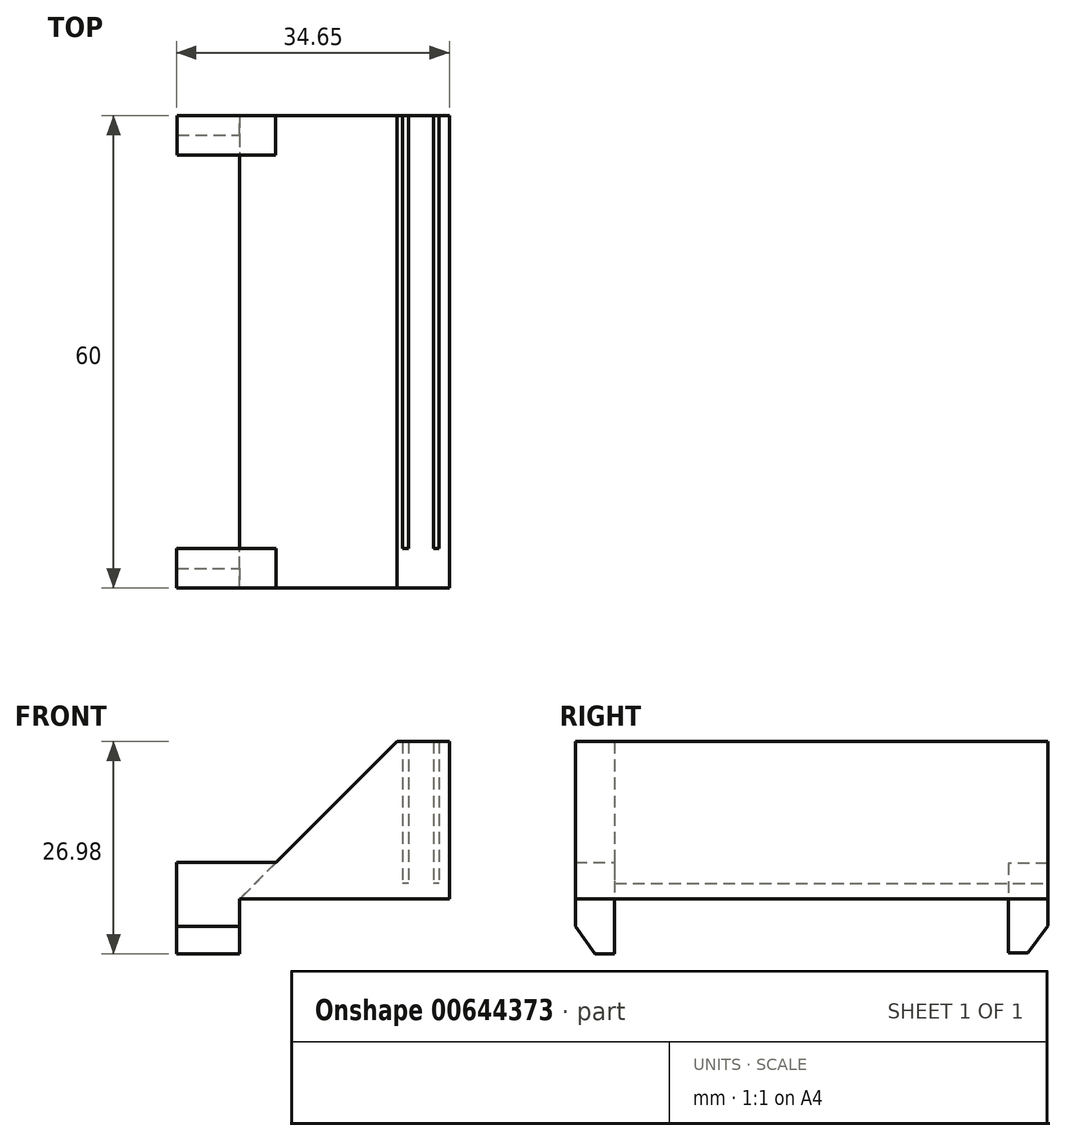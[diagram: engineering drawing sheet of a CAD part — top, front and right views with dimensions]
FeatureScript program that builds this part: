
annotation { "Feature Type Name" : "Feature", "Feature Type Description" : "" }
export const myFeature = defineFeature(function(context is Context, id is Id, definition is map)
    precondition{}
    {
        {
            var Q0;
            Q0=qCreatedBy(makeId("Front.planeOp"),FACE);
            var sketch = newSketch(context, id + "F0", { "sketchPlane" : qUnion([Q0])});
            skLineSegment(sketch, "E0", {"start": v(0.8, 1.7) * mm, "end": v(20.8, 1.7) * mm});
            skLineSegment(sketch, "E1", {"start": v(20.8, 1.7) * mm, "end": v(20.8, 21.7) * mm});
            skLineSegment(sketch, "E2", {"start": v(20.8, 21.7) * mm, "end": v(0.8, 1.7) * mm});
            skSolve(sketch);
        }
        {
            var Q0;
            Q0 = qSketchRegion(id + "F0", true);
            extrude(context, id + "F1", {"entities" : qUnion([Q0]), "depth" : 50 * mm, "offsetDistance" : 25 * mm});
        }
        {
            var Q0;
            Q0=makeQuery(id+"F1.opExtrude","CAP_FACE",FACE,{"disambiguationData":[OSD([sQuery(id+"F0.wireOp",EDGE,"E0"),sQuery(id+"F0.wireOp",EDGE,"E1"),sQuery(id+"F0.wireOp",EDGE,"E2")])],"isStart":true});
            var sketch = newSketch(context, id + "F2", { "sketchPlane" : qUnion([Q0])});
            skLineSegment(sketch, "E3", {"start": v(-20.8, 6.23) * mm, "end": v(7.12, 6.23) * mm});
            skLineSegment(sketch, "E4", {"start": v(7.12, 6.23) * mm, "end": v(7.12, -5.17) * mm});
            skLineSegment(sketch, "E5", {"start": v(7.12, -5.17) * mm, "end": v(-0.8, -5.17) * mm});
            skLineSegment(sketch, "E6", {"start": v(-0.8, -5.17) * mm, "end": v(-0.8, 1.7) * mm});
            skLineSegment(sketch, "E7", {"start": v(-0.8, 1.7) * mm, "end": v(-20.8, 1.7) * mm});
            skLineSegment(sketch, "E8", {"start": v(-20.8, 1.7) * mm, "end": v(-20.8, 6.23) * mm});
            skSolve(sketch);
        }
        {
            var Q0;
            {var subQ1=sQuery(id+"F2.wireOp",EDGE,"E4");Q0=makeQuery(id+"F2.imprint","IMPRINT",FACE,{"disambiguationData":[TD([[makeQuery(id+"F2.imprint","IMPRINT",EDGE,{"derivedFrom":subQ1}),-1.0]])]});}
            var Q1;
            {var subQ4=sQuery(id+"F2.wireOp",EDGE,"E7");Q1=makeQuery(id+"F2.imprint","IMPRINT",FACE,{"disambiguationData":[TD([[makeQuery(id+"F2.imprint","IMPRINT",EDGE,{"derivedFrom":subQ4}),-1.0]])]});}
            extrude(context, id + "F3", {"entities" : qUnion([Q0, Q1]), "operationType" : NewBodyOperationType.ADD, "depth" : 5 * mm, "offsetDistance" : 25 * mm});
        }
        {
            var Q0;
            Q0=makeQuery(id+"F1.opExtrude","CAP_FACE",FACE,{"disambiguationData":[OSD([sQuery(id+"F0.wireOp",EDGE,"E0"),sQuery(id+"F0.wireOp",EDGE,"E1"),sQuery(id+"F0.wireOp",EDGE,"E2")])],"isStart":false});
            var sketch = newSketch(context, id + "F4", { "sketchPlane" : qUnion([Q0])});
            skLineSegment(sketch, "E9", {"start": v(0.8, 1.7) * mm, "end": v(20.8, 1.7) * mm});
            skLineSegment(sketch, "E10", {"start": v(20.8, 1.7) * mm, "end": v(20.8, 6.3) * mm});
            skLineSegment(sketch, "E11", {"start": v(20.8, 6.3) * mm, "end": v(-7.22, 6.3) * mm});
            skLineSegment(sketch, "E12", {"start": v(-7.22, 6.3) * mm, "end": v(-7.22, -5.3) * mm});
            skLineSegment(sketch, "E13", {"start": v(-7.22, -5.3) * mm, "end": v(0.8, -5.3) * mm});
            skLineSegment(sketch, "E14", {"start": v(0.8, -5.3) * mm, "end": v(0.8, 1.7) * mm});
            skSolve(sketch);
        }
        {
            var Q0;
            {var subQ0=sQuery(id+"F4.wireOp",EDGE,"E9");Q0=makeQuery(id+"F4.imprint","IMPRINT",FACE,{"disambiguationData":[TD([[makeQuery(id+"F4.imprint","IMPRINT",EDGE,{"derivedFrom":subQ0}),1.0]])]});}
            var Q1;
            {var subQ1=sQuery(id+"F4.wireOp",EDGE,"E12");Q1=makeQuery(id+"F4.imprint","IMPRINT",FACE,{"disambiguationData":[TD([[makeQuery(id+"F4.imprint","IMPRINT",EDGE,{"derivedFrom":subQ1}),1.0]])]});}
            extrude(context, id + "F5", {"entities" : qUnion([Q0, Q1]), "operationType" : NewBodyOperationType.ADD, "depth" : 5 * mm, "offsetDistance" : 25 * mm});
        }
        {
            var Q0;
            Q0=makeQuery(id+"F5.boolean.opBoolean","MERGE",FACE,{"derivedFrom":[makeQuery(id+"F3.boolean.opBoolean","MERGE",FACE,{"derivedFrom":[makeQuery(id+"F1.opExtrude","SWEPT_FACE",FACE,{"disambiguationData":[OSD([sQuery(id+"F0.wireOp",EDGE,"E1")])]}),makeQuery(id+"F3.opExtrude","SWEPT_FACE",FACE,{"disambiguationData":[OSD([sQuery(id+"F2.wireOp",EDGE,"E8")])]})]}),makeQuery(id+"F5.opExtrude","SWEPT_FACE",FACE,{"disambiguationData":[OSD([sQuery(id+"F4.wireOp",EDGE,"E10")])]})]});
            var sketch = newSketch(context, id + "F6", { "sketchPlane" : qUnion([Q0])});
            skLineSegment(sketch, "E15", {"start": v(-55, 1.7) * mm, "end": v(5, 1.7) * mm});
            skLineSegment(sketch, "E16", {"start": v(5, 1.7) * mm, "end": v(5, 21.7) * mm});
            skLineSegment(sketch, "E17", {"start": v(5, 21.7) * mm, "end": v(-55, 21.7) * mm});
            skLineSegment(sketch, "E18", {"start": v(-55, 21.7) * mm, "end": v(-55, 1.7) * mm});
            skSolve(sketch);
        }
        {
            var Q0;
            Q0 = qSketchRegion(id + "F6", true);
            extrude(context, id + "F7", {"entities" : qUnion([Q0]), "operationType" : NewBodyOperationType.ADD, "depth" : 6.62 * mm, "offsetDistance" : 25 * mm});
        }
        {
            var Q0;
            Q0=makeQuery(id+"F3.opExtrude","SWEPT_FACE",FACE,{"disambiguationData":[OSD([sQuery(id+"F2.wireOp",EDGE,"E6")])]});
            var sketch = newSketch(context, id + "F8", { "sketchPlane" : qUnion([Q0])});
            skLineSegment(sketch, "E19", {"start": v(2.5, -5.17) * mm, "end": v(5, -1.74) * mm});
            skLineSegment(sketch, "E20", {"start": v(5, -1.74) * mm, "end": v(5, -5.17) * mm});
            skLineSegment(sketch, "E21", {"start": v(5, -5.17) * mm, "end": v(2.5, -5.17) * mm});
            skSolve(sketch);
        }
        {
            var Q0;
            Q0 = qSketchRegion(id + "F8", true);
            extrude(context, id + "F9", {"entities" : qUnion([Q0]), "operationType" : NewBodyOperationType.REMOVE, "endBound" : BoundingType.THROUGH_ALL, "oppositeDirection" : true, "depth" : 25 * mm, "offsetDistance" : 25 * mm});
        }
        {
            var Q0;
            Q0=makeQuery(id+"F5.opExtrude","SWEPT_FACE",FACE,{"disambiguationData":[OSD([sQuery(id+"F4.wireOp",EDGE,"E14")])]});
            var sketch = newSketch(context, id + "F10", { "sketchPlane" : qUnion([Q0])});
            skLineSegment(sketch, "E22", {"start": v(-52.5, -5.3) * mm, "end": v(-55, -1.8) * mm});
            skLineSegment(sketch, "E23", {"start": v(-55, -1.8) * mm, "end": v(-55, -5.3) * mm});
            skLineSegment(sketch, "E24", {"start": v(-55, -5.3) * mm, "end": v(-52.5, -5.3) * mm});
            skSolve(sketch);
        }
        {
            var Q0;
            Q0 = qSketchRegion(id + "F10", true);
            extrude(context, id + "F11", {"entities" : qUnion([Q0]), "operationType" : NewBodyOperationType.REMOVE, "endBound" : BoundingType.THROUGH_ALL, "oppositeDirection" : true, "depth" : 25 * mm, "offsetDistance" : 25 * mm});
        }
        {
            var Q0;
            Q0=makeQuery(id+"F7.boolean.opBoolean","MERGE",FACE,{"derivedFrom":[makeQuery(id+"F3.opExtrude","CAP_FACE",FACE,{"disambiguationData":[OSD([sQuery(id+"F2.wireOp",EDGE,"E3"),sQuery(id+"F2.wireOp",EDGE,"E4"),sQuery(id+"F2.wireOp",EDGE,"E5"),sQuery(id+"F2.wireOp",EDGE,"E6"),sQuery(id+"F2.wireOp",EDGE,"E7"),sQuery(id+"F2.wireOp",EDGE,"E8")])],"isStart":false}),makeQuery(id+"F7.opExtrude","SWEPT_FACE",FACE,{"disambiguationData":[OSD([sQuery(id+"F6.wireOp",EDGE,"E16")])]})]});
            var sketch = newSketch(context, id + "F12", { "sketchPlane" : qUnion([Q0])});
            skLineSegment(sketch, "E25.bottom", {"start": v(-26.09, 21.69) * mm, "end": v(-25.39, 21.69) * mm});
            skLineSegment(sketch, "E25.top", {"start": v(-26.09, 3.69) * mm, "end": v(-25.39, 3.69) * mm});
            skLineSegment(sketch, "E25.left", {"start": v(-26.09, 21.69) * mm, "end": v(-26.09, 3.69) * mm});
            skLineSegment(sketch, "E25.right", {"start": v(-25.39, 21.69) * mm, "end": v(-25.39, 3.69) * mm});
            skLineSegment(sketch, "E26.bottom", {"start": v(-22.21, 21.69) * mm, "end": v(-21.51, 21.69) * mm});
            skLineSegment(sketch, "E26.top", {"start": v(-22.21, 3.69) * mm, "end": v(-21.51, 3.69) * mm});
            skLineSegment(sketch, "E26.left", {"start": v(-22.21, 21.69) * mm, "end": v(-22.21, 3.69) * mm});
            skLineSegment(sketch, "E26.right", {"start": v(-21.51, 21.69) * mm, "end": v(-21.51, 3.69) * mm});
            skLineSegment(sketch, "E27", {"start": v(-20.8, 21.7) * mm, "end": v(-38.35, 21.7) * mm, "construction": true});
            skPoint(sketch, "E27.endSnap0", {"position": v(-24.12, 21.7) * mm});
            skSolve(sketch);
        }
        {
            var Q0;
            Q0 = qSketchRegion(id + "F12", true);
            extrude(context, id + "F13", {"entities" : qUnion([Q0]), "operationType" : NewBodyOperationType.REMOVE, "oppositeDirection" : true, "depth" : 55 * mm, "offsetDistance" : 25 * mm});
        }
        {
            var Q0;
            Q0=makeQuery(id+"F1.opExtrude","CAP_FACE",FACE,{"disambiguationData":[OSD([sQuery(id+"F0.wireOp",EDGE,"E0"),sQuery(id+"F0.wireOp",EDGE,"E1"),sQuery(id+"F0.wireOp",EDGE,"E2")])],"isStart":false});
            extrude(context, id + "F14", {"entities" : qUnion([Q0]), "operationType" : NewBodyOperationType.ADD, "depth" : 5 * mm, "offsetDistance" : 25 * mm});
        }
        {
            var Q0;
            Q0=makeQuery(id+"F1.opExtrude","CAP_FACE",FACE,{"disambiguationData":[OSD([sQuery(id+"F0.wireOp",EDGE,"E0"),sQuery(id+"F0.wireOp",EDGE,"E1"),sQuery(id+"F0.wireOp",EDGE,"E2")])],"isStart":true});
            extrude(context, id + "F15", {"entities" : qUnion([Q0]), "operationType" : NewBodyOperationType.ADD, "depth" : 5 * mm, "offsetDistance" : 25 * mm});
        }
        {
            var Q0;
            Q0=makeQuery(id+"F7.opExtrude","CAP_FACE",FACE,{"disambiguationData":[OSD([sQuery(id+"F6.wireOp",EDGE,"E15"),sQuery(id+"F6.wireOp",EDGE,"E16"),sQuery(id+"F6.wireOp",EDGE,"E17"),sQuery(id+"F6.wireOp",EDGE,"E18")])],"isStart":false});
            var sketch = newSketch(context, id + "F16", { "sketchPlane" : qUnion([Q0])});
            skText(sketch, "E28", { "text": "FT Multi Tool v1", "fontName": "RobotoSlab-Regular.ttf"});
            const initialGuessF16  = {"E28": [-0.04622, 0.01522, 1, 0, 0.00474]};
            skSetInitialGuess(sketch, initialGuessF16);
            skSolve(sketch);
        }
        {
            var Q0;
            Q0 = qConstructionFilter(qBodyType(qCreatedBy(id + "F16" ,EDGE), BodyType.WIRE), ConstructionObject.NO);
            extrude(context, id + "F17", {"bodyType" : ToolBodyType.SURFACE, "surfaceEntities" : qUnion([Q0]), "depth" : 0.19 * mm, "offsetDistance" : 25 * mm});
        }
    });
